# Revit family: CENTUM Führungsschiene für Gleitlager, hängend für HEA 80-120
name_source: partatom
category: HLS-Bauteile
units: mm (PartAtom-declared; Revit-internal decimal feet)

## family parameters
Arbeitsebenenbasiert = Ja
Beim Laden mit Abzugskörper schneiden = Nein
Bemaßung runder Anschluss = Durchmesser verwenden
Beschriftungsausrichtung beibehalten = Nein
Gemeinsam genutzt = Ja
Immer vertikal = Nein
Klassifizierung = Keine
Raumberechnungspunkt = Nein
Teiletyp = Normal

## types (1)
- Führungsschiene für Gleitlager, hängend für HEA80-120
    Artikelnummer = 1663080120
    Benötigtis Zubehör = CENTUM Spannklaue Typ LR M12
    EAN = 4250928459480
    Einsatzgebiet = Befestigung von Gleitlagern an Stahlträgern
    Fabrikat = MEFA
    Gewicht = 2.40 kg
    Gewicht pro Bauteil = 2.40 kg
    Hinweis = Lieferung erfolgt paarweise
    Kurztext1 = Führungsschiene für Gleitlager hängend
    Kurztext2 = für HEA 80-120
    Lochdurchmesser = 14x40
    Material = Stahl
    Materialname = S235
    Mengeneinheit = Set
    Oberflaeche = Feuerverzinkt
    Typ = hängend
    Vorgabe-Ansicht = 1219 mm
    für Träger HEA = 80-120
    max. zul. Last (gesamt) = 6 kN
    vpe = 1
